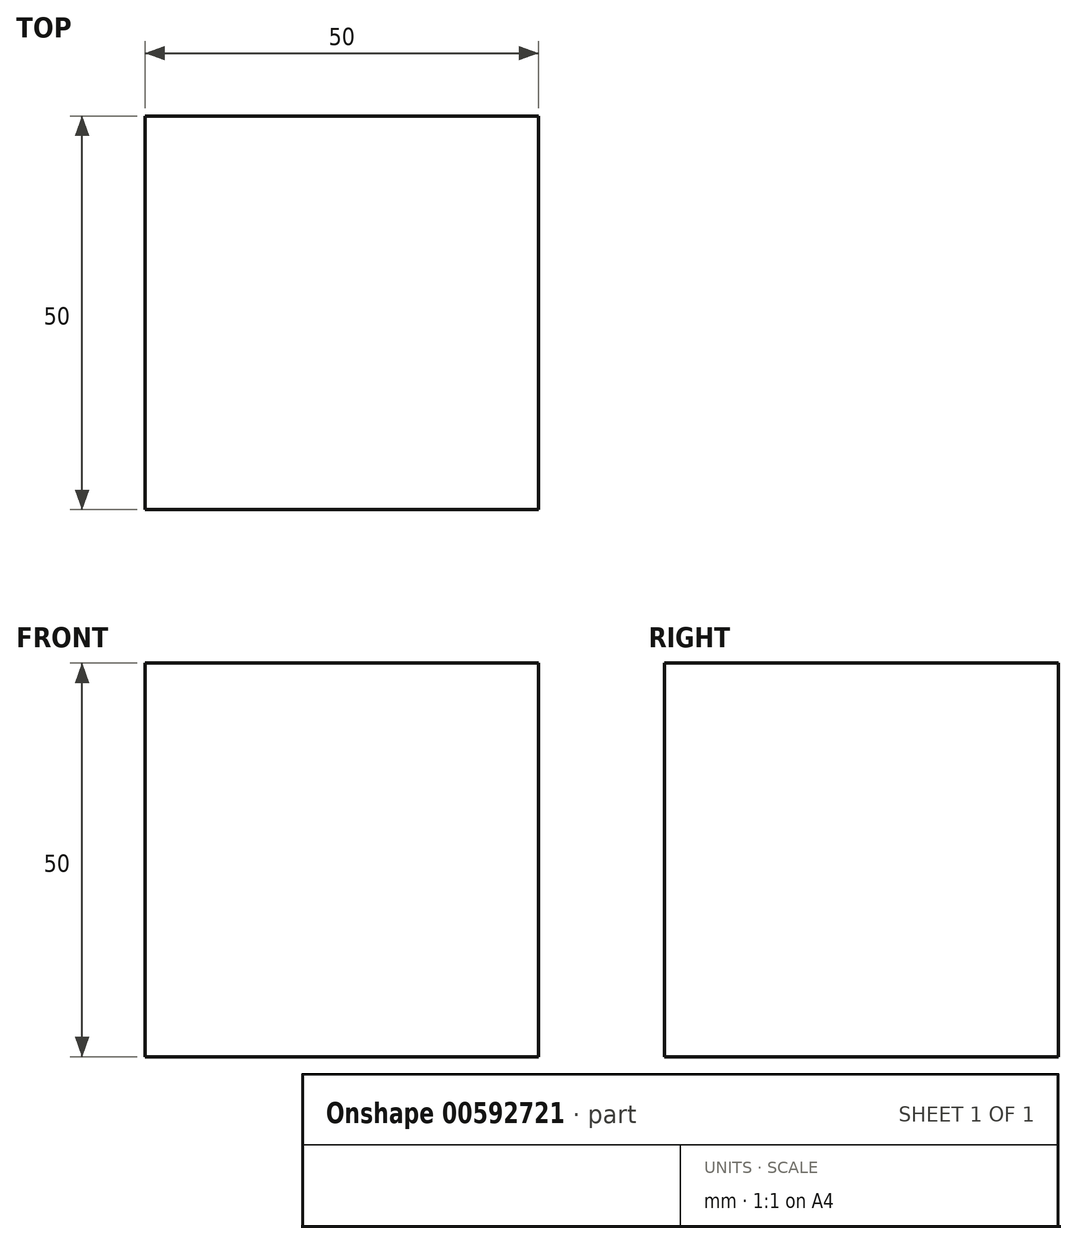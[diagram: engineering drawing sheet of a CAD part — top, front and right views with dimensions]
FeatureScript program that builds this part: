
annotation { "Feature Type Name" : "Feature", "Feature Type Description" : "" }
export const myFeature = defineFeature(function(context is Context, id is Id, definition is map)
    precondition{}
    {
        {
            var Q0;
            Q0=qCreatedBy(makeId("Top.planeOp"),FACE);
            var sketch = newSketch(context, id + "F0", { "sketchPlane" : qUnion([Q0])});
            skLineSegment(sketch, "E0.bottom", {"start": v(-25, -25) * mm, "end": v(25, -25) * mm});
            skLineSegment(sketch, "E0.top", {"start": v(-25, 25) * mm, "end": v(25, 25) * mm});
            skLineSegment(sketch, "E0.left", {"start": v(-25, -25) * mm, "end": v(-25, 25) * mm});
            skLineSegment(sketch, "E0.right", {"start": v(25, -25) * mm, "end": v(25, 25) * mm});
            skPoint(sketch, "E0.middle", {"position": v(0, 0) * mm});
            skSolve(sketch);
        }
        {
            var Q0;
            Q0=makeQuery(id+"F0.imprint","IMPRINT",FACE,{"disambiguationData":[TD([[makeQuery(id+"F0.imprint","IMPRINT",EDGE,{"derivedFrom":sQuery(id+"F0.wireOp",EDGE,"E0.bottom")}),1.0]])]});
            extrude(context, id + "F1", {"entities" : qUnion([Q0]), "depth" : 25 * mm, "offsetDistance" : 25 * mm, "hasSecondDirection" : true, "secondDirectionOppositeDirection" : true, "secondDirectionDepth" : 25 * mm});
        }
        {
            var Q0;
            Q0=qCreatedBy(makeId("Top.planeOp"),FACE);
            var sketch = newSketch(context, id + "F2", { "sketchPlane" : qUnion([Q0])});
            skCircle(sketch, "E1", {"center": v(0, 0) * mm, "radius": 18.93 * mm});
            skSolve(sketch);
        }
        {
            var Q0;
            Q0=sQuery(id+"F2.wireOp",EDGE,"E1");
            extrude(context, id + "F3", {"bodyType" : ToolBodyType.SURFACE, "surfaceEntities" : qUnion([Q0]), "depth" : 25 * mm, "offsetDistance" : 25 * mm, "hasSecondDirection" : true, "secondDirectionOppositeDirection" : true, "secondDirectionDepth" : 25 * mm});
        }
    });
